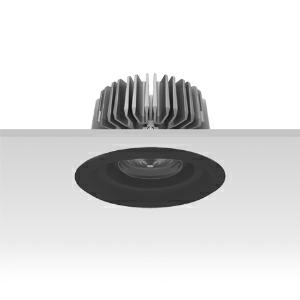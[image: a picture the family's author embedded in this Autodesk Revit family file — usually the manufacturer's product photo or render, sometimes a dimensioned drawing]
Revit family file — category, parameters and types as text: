
# Revit family: 3f_filippi_-_3f_reno_nero_ampio_3f_filippi_-_31271_-_3f_reno_150_bk_3000-930_dali_wide
name_source: partatom
category: Lighting Fixtures
units: mm (PartAtom-declared; Revit-internal decimal feet)

## family parameters
Cut with Voids When Loaded = No
Host = Face
Light Source = No
Part Type = Normal
Room Calculation Point = No
Round Connector Dimension = Use Diameter
Shared = No

## types (1)
- 3F Filippi - 3F Reno Nero Ampio (1 x LED, 2393 lm, 37 W, 3000 K)
    Apparent Load = 37 VA
    Approval mark = CE
    CIE Flux Codes = 82 99 100 100 100
    Color Rendering = 90
    Color Temperature = 3000 K
    Control Gear = Electronic transformer
    Default Elevation = 1800 mm
    Description = ILLUMINOTECHNICAL
Luminous efficiency 100% (DLOR 100%, ULOR 0%).
Initial luminous flux of the luminaire 2393 lm.
Direct symmetric wide distribution.
Installation Interdistance Transv.D = 1.55 x hu - Long.D = 1.55 x hu.
Tabular UGR (CIE 117 - 4H-8H; S=0.25H; 70/50/20): RUG 21.8 - 21.8.
Beam angle: 84° - 83°.
Luminous efficacy 65 lm/W.
Lifetime (L90/B10): 30000 h. (tq+25°C)
Lifetime (L85/B10): 50000 h. (tq+25°C)
Lifetime (L70/B10): 80000 h. (tq+25°C)
Sudden decreased luminous flux after 50000 hours: 0% (C0).
Photobiological safety in compliance with IEC/TR 62778: RG0 risk exempt, (IEC 62471).
In compliance with IEC/EN 62722-2-1 - IEC/EN 62717 standards.

SOURCE
Compact LED module 3000/930.
Energy efficiency class (UE 2019/2020 - UE 2019/2015): F.
CIE 13.3 Colour rendering index: CRI >90 (R9 >50%).
IES TM-30 Fidelity Index: Rf = 92 Rg = 101.
CCT nominal colour temperature 3000 K.
Colour initial tolerance (MacAdam): SDCM 3.
Zhaga Book 3 compliant.

MECHANICAL
Passive heat dissipator in die-casting aluminium, oversized, for optimum thermal management of the LED module.
Parabolic element with graduated/concentric rings in black polycarbonate.
Transparent external lens with glossy and satin differentiated surfaces, with a cooling and anti-insect system in methacrylate (PMMA).
Fastening spring clips in stainless steel.
Dimensions: diameter 166 mm, height 107 mm. Weight 1.39 kg.
IP44 protection degree for exposed part, IP20 for recessed part.
Mechanical strength to impacts IK04 (0.5 joule).
Glow-wire test resistance 650°C.

ELECTRICAL
Wiring on a separate unit.
Halogen Free DALI-2 DATI (Parts 251, 252, 253), PUSH-DIM, electronic wiring 230V-50/60Hz, power factor 0.97 at full load, THD <25%, constant output current, SELV, class II, 1 driver, 1 DALI addresse.
Power of the luminaire 37 W.
ENEC - CE.
SAFE FLICKER: PstLM=<1 and SVM=<0.4 (IEC TR 61547-1 and IEC TR 63158), to ensure a more comfortable and safe light.
Luminaire compliant with EN 60598-2-22 for power supply from a centralised emergency system CPSS (Central Power Supply System), not incorporated in the luminaire - high risk areas excluded. The default power and flux are 100% in AC and 100% in DC.
Ambient temperature from 0°C to +25°C.
Temperature class T6 max 85°C.
Relative humidity UR: <85%.

INSTALLATION
Pull-up recessed fitting.
False ceiling carving: 150 mm.
All accessories dedicated to this product are available on the Catalog and on our website www.3F-Filippi.com.

APPLICATIONS
Environments: architectural, commercial, exhibition areas, transit areas, corridors, shops, display windows, service areas.
In false ceilings with narrow voids.

LIGHT MANAGEMENT
Recommended minimum setting: 10%.
The luminaire, equipped with (DALI-2 DATI) driver, can be controlled manually with 3F Easy Dim technology or automatically/manually with wired or wireless DALI/D2D control systems.
The D2D driver guarantees interoperability with other devices with the same certification by making the following information available:
Device Data (Part 251), Energy Report (Part 252), Diagnosis & Maintenance (Part 253).
In electrical systems without a regulation system (manual or automatic) and DALI bus, a suitable jumper must be made on the DA-DA terminals of the appliance.

WARNING
Luminaire designed for disposal/recycling at end-of-life.
Replaceable (LED only) light source by a professional. Replaceable control gear by a professional.
    Height = 0 mm  [stored 0 ft]
    Lamp = 1 x LED
    Lamp Light Flux = 2393 lm
    Lamp Power = 37 W
    Lamp count = 1
    Length = 166 mm
    Lifetime = 50000 h
    Luminous efficacy = 65 lm/W
    Manufacturer = 3F Filippi
    ModVariant = No
    Model = 3F Filippi - 31271 - 3F Reno 150 BK 3000-930 DALI WIDE
    Mounting Place = Ceiling
    Mounting Type = Recessed
    Number of Poles = 1
    OnlyDefault = Yes
    Power Factor = 1
    Product Name = 3F Filippi - 3F Reno Nero Ampio
    Product group = recessed luminaire
    ProductGroupID = 4
    Protection Class = Protection class II
    Protection Degree = IP 20
    RLX_Detail_Level = 1
    RLX_Emergency_Light_Flux = 0 lm
    RLX_Emergency_Type = 0
    RLX_Emergency_Type_DB = No
    RlxData = <blob elided: 85549 chars, md5=62dda7d0>
    Socket = socket
    Standby Power = 0 W
    System Light Flux = 2393 lm
    System Power = 37 W
    Type Comments = Product without accessories
    Type Image = 3ffilippi_3f_reno_150_ampio_bk_3000_4000.jpg
    URL = http://relux.com
    VarID = ---
    Voltage = 0 V
    Weight = 0.00 kg
    Width = 0 mm  [stored 0 ft]

note: [stored X ft] marks values corroborated as IEEE doubles in the binary element streams (Revit-internal decimal feet)

## geometry (parser evidence)
native form markers: Blend x4, Sweep x11
no freeform markers — native parametric forms only
